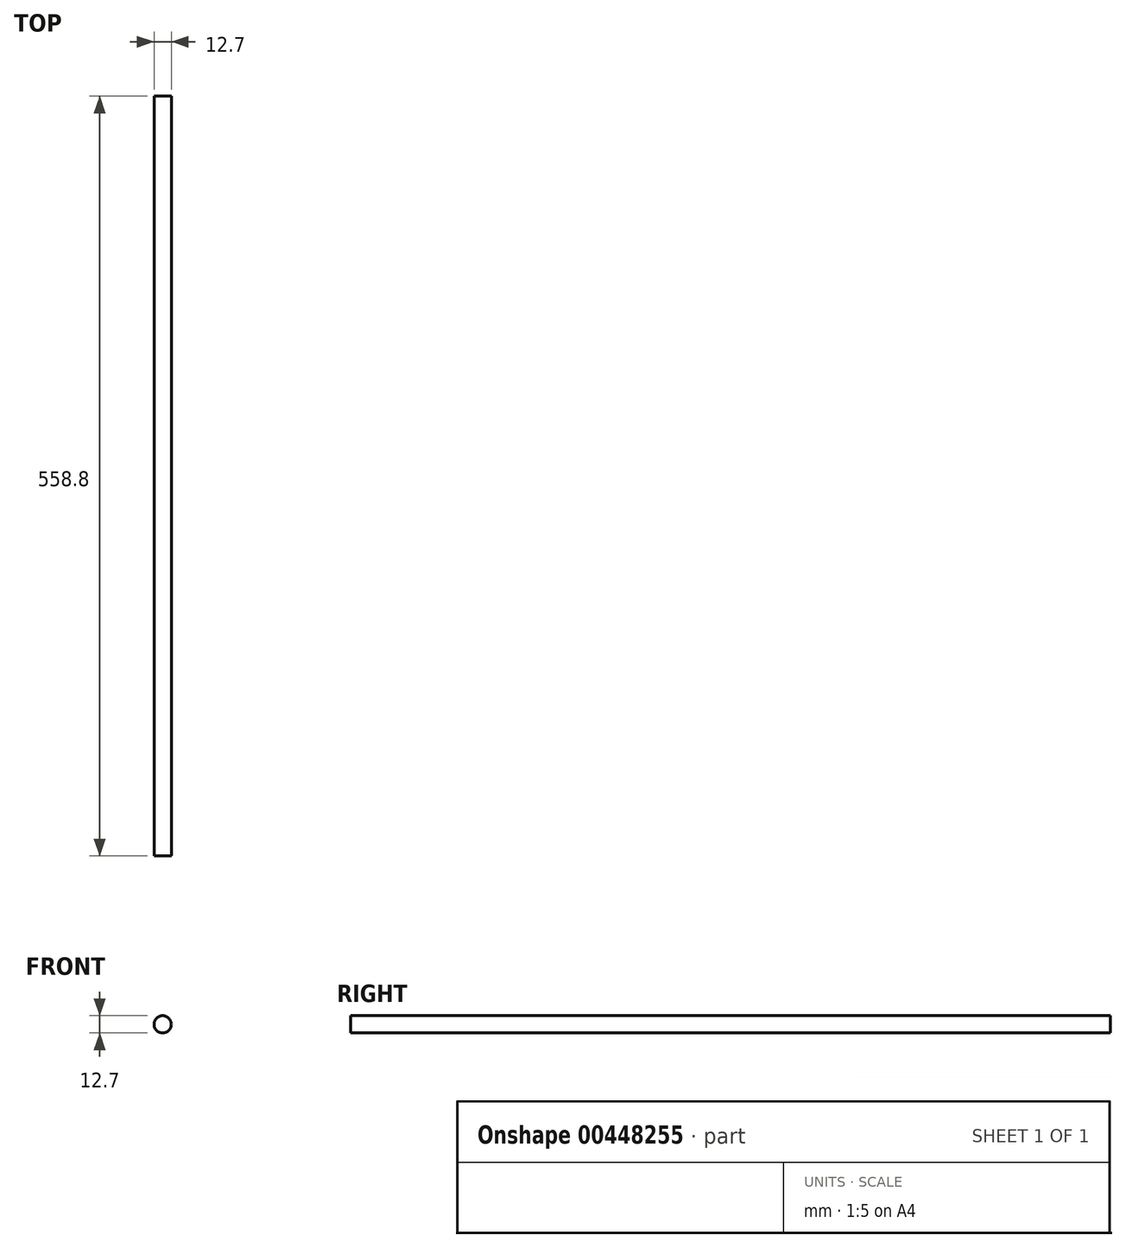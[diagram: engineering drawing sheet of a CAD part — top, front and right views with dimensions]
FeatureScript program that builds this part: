
annotation { "Feature Type Name" : "Feature", "Feature Type Description" : "" }
export const myFeature = defineFeature(function(context is Context, id is Id, definition is map)
    precondition{}
    {
        {
            var Q0;
            Q0=qCreatedBy(makeId("Front.planeOp"),FACE);
            var sketch = newSketch(context, id + "F0", { "sketchPlane" : qUnion([Q0])});
            skCircle(sketch, "E0", {"center": v(0, 0) * mm, "radius": 6.35 * mm});
            skSolve(sketch);
        }
        {
            var Q0;
            Q0=makeQuery(id+"F0.imprint","IMPRINT",FACE,{"disambiguationData":[TD([[makeQuery(id+"F0.imprint","IMPRINT",EDGE,{"derivedFrom":sQuery(id+"F0.wireOp",EDGE,"E0")}),1.0]])]});
            extrude(context, id + "F1", {"entities" : qUnion([Q0]), "depth" : 558.8 * mm});
        }
    });
